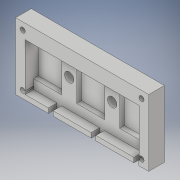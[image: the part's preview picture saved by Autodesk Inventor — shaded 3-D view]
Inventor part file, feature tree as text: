
AUTODESK INVENTOR PART (.ipt)
format: ipt  version: 2018 (Build 220112000, 112)  size: 208,384 bytes
history: native  units: in
note: dims shown in document units (in); Inventor stores cm internally (conversion verified against a paired STEP export)
features: extrude x5, sketch x4, hole x2, pattern_linear x1, projected_geometry x1
ambient origin geometry x8: Origin, YZ Plane, XZ Plane, XY Plane, X Axis, Y Axis, Z Axis, Center Point
bodies: Solid1 (feature_tree)
feature tree (13):
  sketch  "Sketch1"  dims[d0=7.0in d1=3.5in]
  extrude  "Extrusion1"  Depth=3.5in
  extrude  "Extrusion2"  Depth=2.0in
  extrude  "Extrusion3"  Depth=0.5in
  extrude  "Extrusion4"  Depth=0.7in TaperAngle=0.0deg
  pattern_linear  "Rectangular Pattern1"  Spacing1=0.125in  [1 undecoded]
  hole  "Hole2"  [1 undecoded]
  extrude  "Extrusion5"  Depth=0.25in
  sketch  "Sketch2"  dims[d2=1.475in d3=2.0in]
  sketch  "Sketch3"  dims[d4=0.5in d5=0.5in]
  hole  "Hole1"  [1 undecoded]
  sketch  "Sketch4"  dims[d6=0.5in d7=0.7in d8=0.0in d9=0.125in d10=0.0in d11=0.25in d12=0.0in d13=0.25in d14=0.25in d15=0.0in d16=1.1811in d18=2.25in d19=0.266in d20=0.75in d21=0.375in d22=0.25in d23=0.5635in d24=1.0in d25=0.0in d26=0.5in d27=1.0in d28=0.0in]
  projected_geometry  "Projected Loop1"
note: 3 required parameter values undecoded (feature->parameter linkage not recoverable at this tier; creation-order binding heuristic only, values carry confidence <= 0.55)
